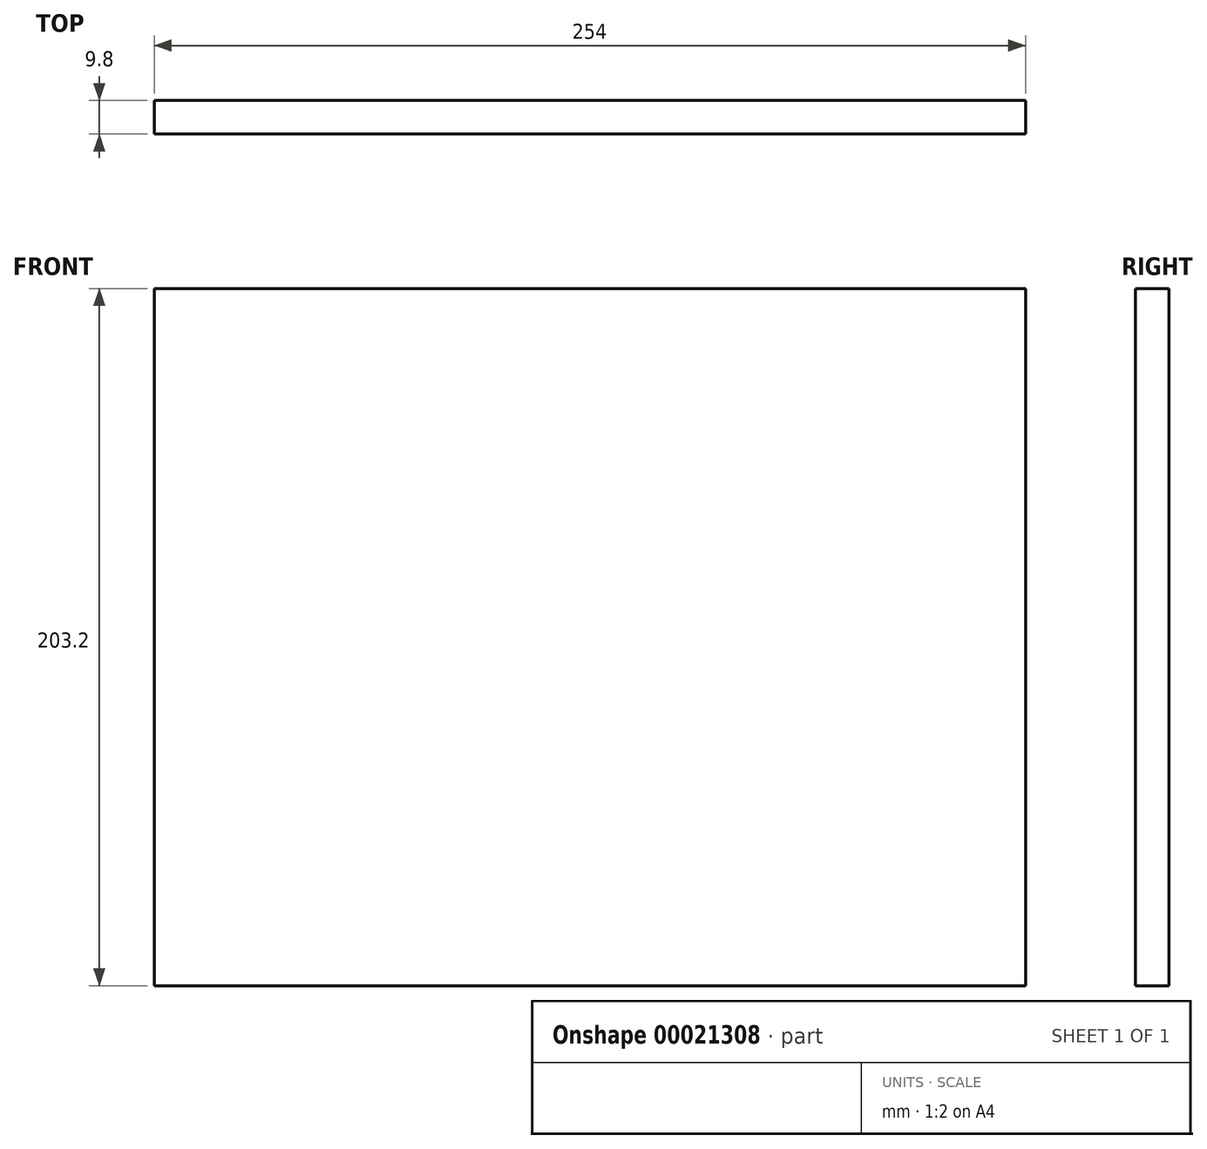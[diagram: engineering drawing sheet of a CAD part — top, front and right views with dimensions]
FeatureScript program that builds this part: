
annotation { "Feature Type Name" : "Feature", "Feature Type Description" : "" }
export const myFeature = defineFeature(function(context is Context, id is Id, definition is map)
    precondition{}
    {
        {
            var Q0;
            Q0=qCreatedBy(makeId("Front.planeOp"),FACE);
            var sketch = newSketch(context, id + "F0", { "sketchPlane" : qUnion([Q0])});
            skLineSegment(sketch, "E0.bottom", {"start": v(-254, 0) * mm, "end": v(0, 0) * mm});
            skLineSegment(sketch, "E0.top", {"start": v(-254, -203.2) * mm, "end": v(0, -203.2) * mm});
            skLineSegment(sketch, "E0.left", {"start": v(-254, 0) * mm, "end": v(-254, -203.2) * mm});
            skLineSegment(sketch, "E0.right", {"start": v(0, 0) * mm, "end": v(0, -203.2) * mm});
            skSolve(sketch);
        }
        {
            var Q0;
            Q0=makeQuery(id+"F0.imprint","IMPRINT",FACE,{"disambiguationData":[TD([[makeQuery(id+"F0.imprint","IMPRINT",EDGE,{"derivedFrom":sQuery(id+"F0.wireOp",EDGE,"E0.bottom")}),-1.0]])]});
            extrude(context, id + "F1", {"entities" : qUnion([Q0]), "depth" : 9.8 * mm});
        }
    });
